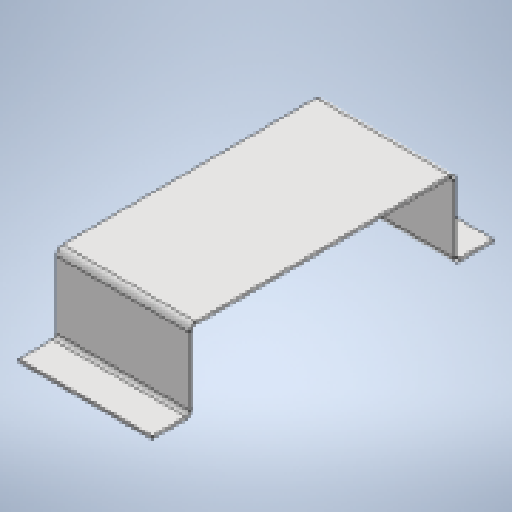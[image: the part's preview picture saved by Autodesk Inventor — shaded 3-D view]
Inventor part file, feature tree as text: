
AUTODESK INVENTOR PART (.ipt)
format: ipt  version: 2025.1 (Build 291241020, 241B)  size: 205,312 bytes
history: native  units: mm
features: sheet_metal_op x7, other x5, sketch x3
ambient origin geometry x8: Origin, YZ Plane, XZ Plane, XY Plane, X Axis, Y Axis, Z Axis, Center Point
bodies: Solid1 (feature_tree)
feature tree (15):
  sheet_metal_op  "Face1"
  other  "A-Side Definition"
  sheet_metal_op  "Flange1"
  sheet_metal_op  "Flange2"
  sketch  "Sketch1"  dims[d0=140.0mm]
  other  "Plate1"
  sketch  "Sketch3"  dims[d1=270.0mm]
  other  "Plate2"
  sheet_metal_op  "Bend1"
  sheet_metal_op  "Corner1"
  sketch  "Sketch4"  dims[d2=2.0mm d6=2.0mm d7=1.0mm d8=4.0mm d9=2.75mm d10=50.0mm d11=90.0deg d12=2.75mm d13=8.0mm d14=2.0mm d15=2.75mm d16=2.0mm d17=1.0mm d18=4.0mm d19=2.75mm d20=15.0mm d21=90.0deg d22=2.75mm d23=8.0mm d24=2.0mm d25=2.75mm]
  other  "Plate3"
  sheet_metal_op  "Bend2"
  sheet_metal_op  "Corner2"
  other  "Definition1"
